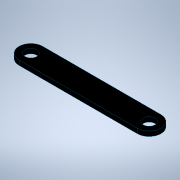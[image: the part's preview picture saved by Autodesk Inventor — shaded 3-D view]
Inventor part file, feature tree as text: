
AUTODESK INVENTOR PART (.ipt)
format: ipt  version: 2020.1 (Build 241239000, 239)  size: 117,760 bytes
history: native  units: in
note: dims shown in document units (in); Inventor stores cm internally (conversion verified against a paired STEP export)
features: extrude x1, sketch x1
ambient origin geometry x8: Origin, YZ Plane, XZ Plane, XY Plane, X Axis, Y Axis, Z Axis, Center Point
bodies: Solid1 (feature_tree)
feature tree (2):
  extrude  "Extrusion1"  Depth=10.0in
  sketch  "Sketch1"  dims[d0=50.0in d1=10.0in d2=5.0in d3=5.0in d4=2.0in d5=0.0in]
